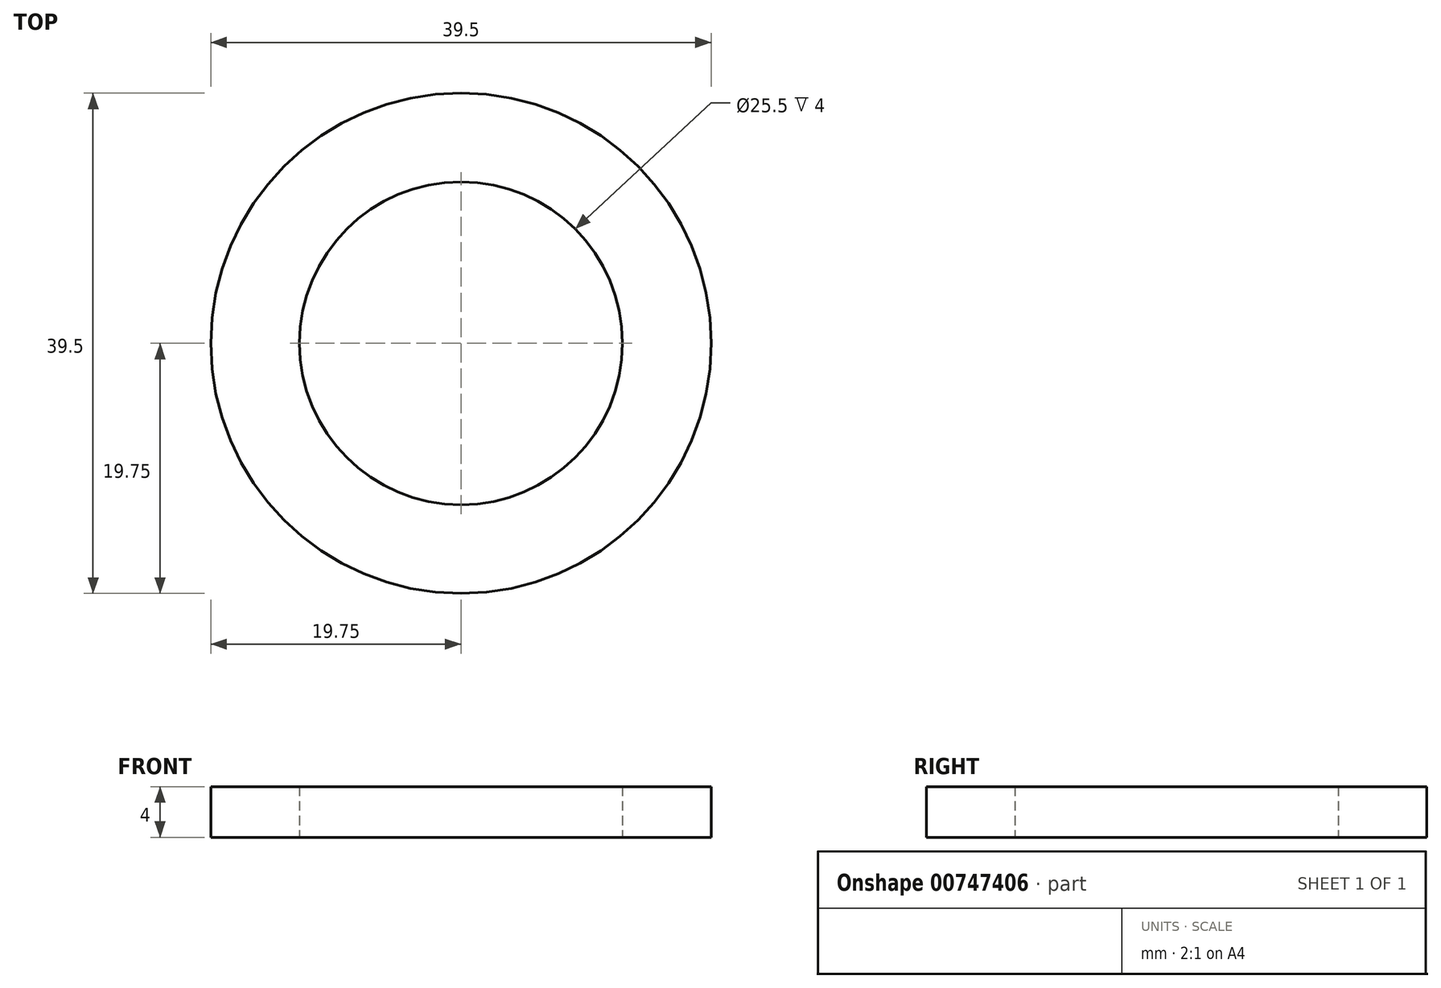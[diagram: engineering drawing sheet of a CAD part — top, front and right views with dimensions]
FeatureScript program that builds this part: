
annotation { "Feature Type Name" : "Feature", "Feature Type Description" : "" }
export const myFeature = defineFeature(function(context is Context, id is Id, definition is map)
    precondition{}
    {
        {
            var Q0;
            Q0=qCreatedBy(makeId("Top.planeOp"),FACE);
            var sketch = newSketch(context, id + "F0", { "sketchPlane" : qUnion([Q0])});
            skCircle(sketch, "E0", {"center": v(0, 0) * mm, "radius": 19.75 * mm});
            skCircle(sketch, "E1", {"center": v(0, 0) * mm, "radius": 12.75 * mm});
            skSolve(sketch);
        }
        {
            var Q0;
            Q0 = qSketchRegion(id + "F0", true);
            extrude(context, id + "F1", {"entities" : qUnion([Q0]), "depth" : 4 * mm, "offsetDistance" : 25 * mm});
        }
    });
